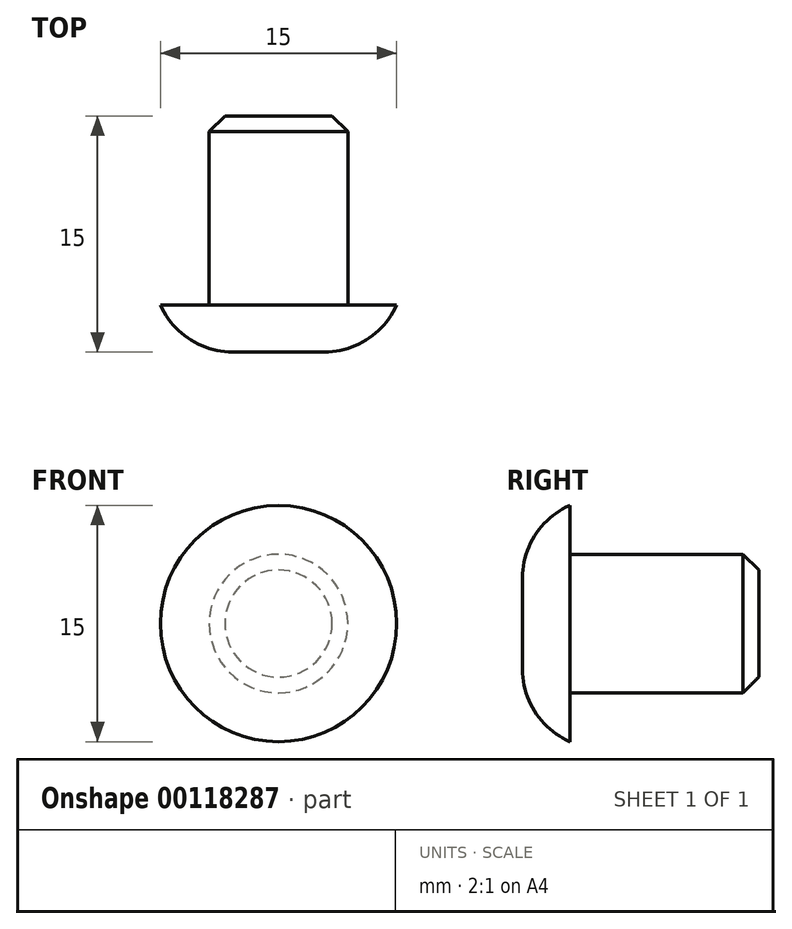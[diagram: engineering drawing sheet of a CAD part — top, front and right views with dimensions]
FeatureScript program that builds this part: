
annotation { "Feature Type Name" : "Feature", "Feature Type Description" : "" }
export const myFeature = defineFeature(function(context is Context, id is Id, definition is map)
    precondition{}
    {
        {
            var Q0;
            Q0=qCreatedBy(makeId("Front.planeOp"),FACE);
            var sketch = newSketch(context, id + "F0", { "sketchPlane" : qUnion([Q0])});
            skCircle(sketch, "E0", {"center": v(0, 0) * mm, "radius": 4.4 * mm});
            skSolve(sketch);
        }
        {
            var Q0;
            Q0 = qSketchRegion(id + "F0", true);
            var Q1;
            Q1=makeQuery(id+"F0.imprint","IMPRINT",FACE,{"disambiguationData":[TD([[makeQuery(id+"F0.imprint","IMPRINT",EDGE,{"derivedFrom":sQuery(id+"F0.wireOp",EDGE,"E0")}),1.0]])]});
            extrude(context, id + "F1", {"entities" : qUnion([Q0, Q1]), "depth" : 12 * mm});
        }
        {
            var Q0;
            Q0=makeQuery(id+"F1.opExtrude","CAP_FACE",FACE,{"disambiguationData":[OSD([sQuery(id+"F0.wireOp",EDGE,"E0")])],"isStart":false});
            var sketch = newSketch(context, id + "F2", { "sketchPlane" : qUnion([Q0])});
            skCircle(sketch, "E1", {"center": v(0, 0) * mm, "radius": 7.5 * mm});
            skSolve(sketch);
        }
        {
            var Q0;
            Q0 = qSketchRegion(id + "F2", true);
            var Q1;
            Q1=makeQuery(id+"F2.imprint","IMPRINT",FACE,{"disambiguationData":[TD([[makeQuery(id+"F2.imprint","IMPRINT",EDGE,{"derivedFrom":sQuery(id+"F2.wireOp",EDGE,"E1")}),1.0]])]});
            extrude(context, id + "F3", {"entities" : qUnion([Q0, Q1]), "operationType" : NewBodyOperationType.ADD, "depth" : 3 * mm});
        }
        {
            var Q0;
            Q0=makeQuery(id+"F3.opExtrude","CAP_EDGE",EDGE,{"disambiguationData":[OSD([sQuery(id+"F2.wireOp",EDGE,"E1")])],"isStart":false});
            fillet(context, id + "F4", {"entities" : qUnion([Q0]), "radius" : 5 * mm, "tangentPropagation" : true, "allowEdgeOverflow" : false});
        }
        {
            var Q0;
            Q0=makeQuery(id+"F1.opExtrude","CAP_EDGE",EDGE,{"disambiguationData":[OSD([sQuery(id+"F0.wireOp",EDGE,"E0")])],"isStart":true});
            chamfer(context, id + "F5", {"entities" : qUnion([Q0]), "width" : 1 * mm, "tangentPropagation" : true});
        }
    });
